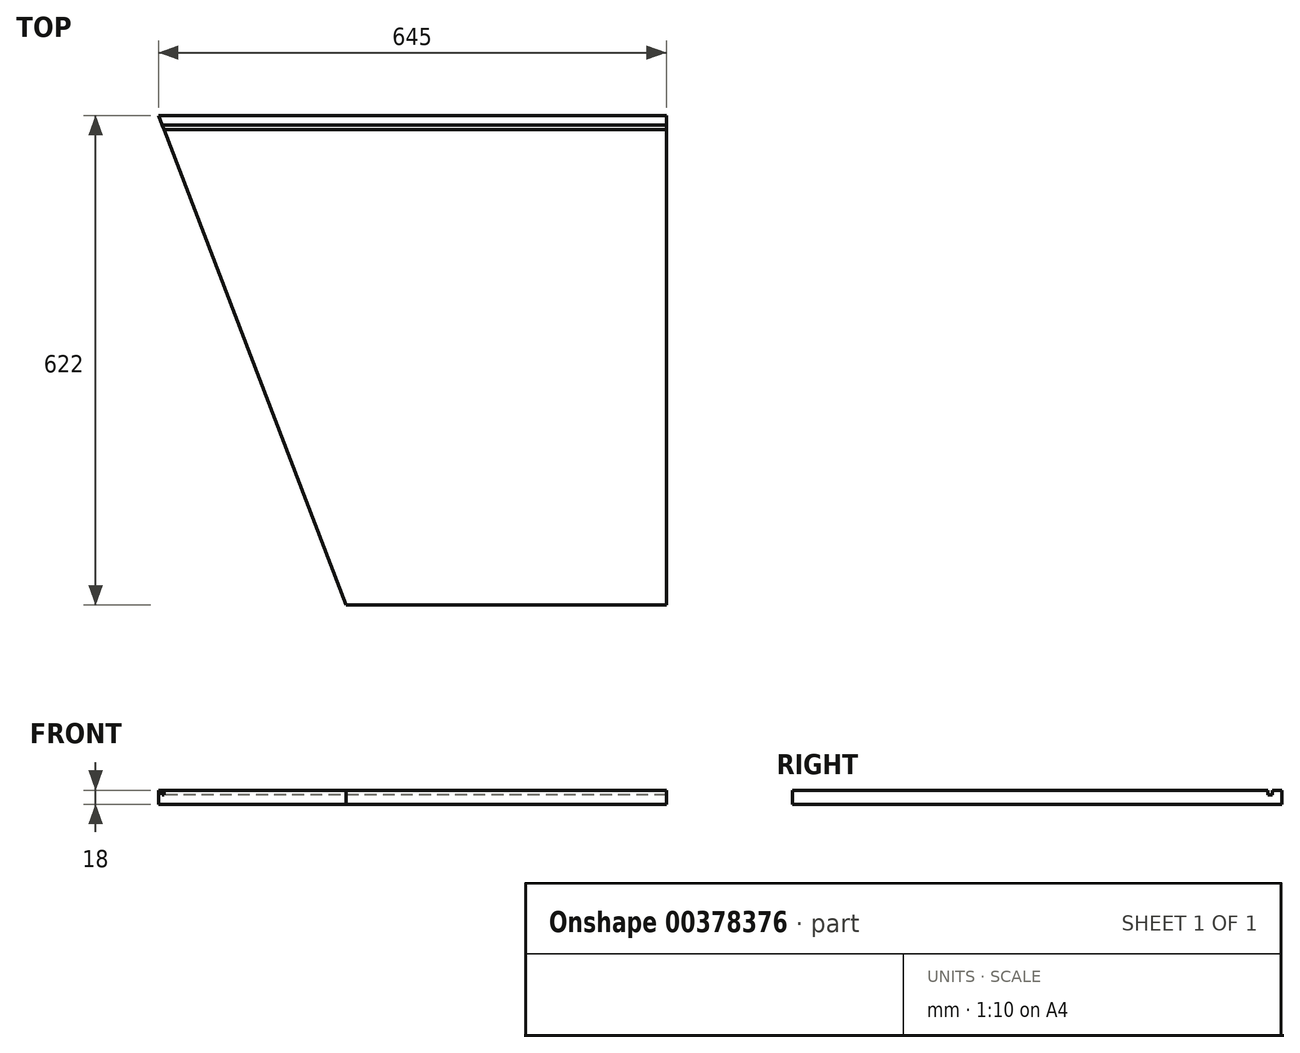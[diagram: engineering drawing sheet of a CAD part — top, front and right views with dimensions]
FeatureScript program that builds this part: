
annotation { "Feature Type Name" : "Feature", "Feature Type Description" : "" }
export const myFeature = defineFeature(function(context is Context, id is Id, definition is map)
    precondition{}
    {
        {
            var Q0;
            Q0=qCreatedBy(makeId("Top.planeOp"),FACE);
            var sketch = newSketch(context, id + "F0", { "sketchPlane" : qUnion([Q0])});
            skLineSegment(sketch, "E0.bottom", {"start": v(322.5, 311) * mm, "end": v(-322.5, 311) * mm});
            skLineSegment(sketch, "E0.top", {"start": v(322.5, -311) * mm, "end": v(-84.44, -311) * mm});
            skLineSegment(sketch, "E0.left", {"start": v(322.5, 311) * mm, "end": v(322.5, -311) * mm});
            skPoint(sketch, "E0.middle", {"position": v(0, 0) * mm});
            skLineSegment(sketch, "E1", {"start": v(-322.5, 311) * mm, "end": v(-84.44, -311) * mm});
            skSolve(sketch);
        }
        {
            var Q0;
            Q0 = qSketchRegion(id + "F0", true);
            extrude(context, id + "F1", {"entities" : qUnion([Q0]), "depth" : 18 * mm});
        }
        {
            var Q0;
            Q0=makeQuery(id+"F1.opExtrude","CAP_FACE",FACE,{"disambiguationData":[OSD([sQuery(id+"F0.wireOp",EDGE,"E0.bottom"),sQuery(id+"F0.wireOp",EDGE,"E0.top"),sQuery(id+"F0.wireOp",EDGE,"E0.left"),sQuery(id+"F0.wireOp",EDGE,"E1")])],"isStart":false});
            var sketch = newSketch(context, id + "F2", { "sketchPlane" : qUnion([Q0])});
            skLineSegment(sketch, "E2.bottom", {"start": v(322.5, 299) * mm, "end": v(-317.9, 299) * mm});
            skLineSegment(sketch, "E2.top", {"start": v(322.5, 293) * mm, "end": v(-317.9, 293) * mm});
            skLineSegment(sketch, "E2.left", {"start": v(322.5, 299) * mm, "end": v(322.5, 293) * mm});
            skLineSegment(sketch, "E2.right", {"start": v(-317.9, 299) * mm, "end": v(-317.9, 293) * mm});
            skSolve(sketch);
        }
        {
            var Q0;
            Q0 = qSketchRegion(id + "F2", true);
            extrude(context, id + "F3", {"entities" : qUnion([Q0]), "operationType" : NewBodyOperationType.REMOVE, "oppositeDirection" : true, "depth" : 6 * mm});
        }
    });
